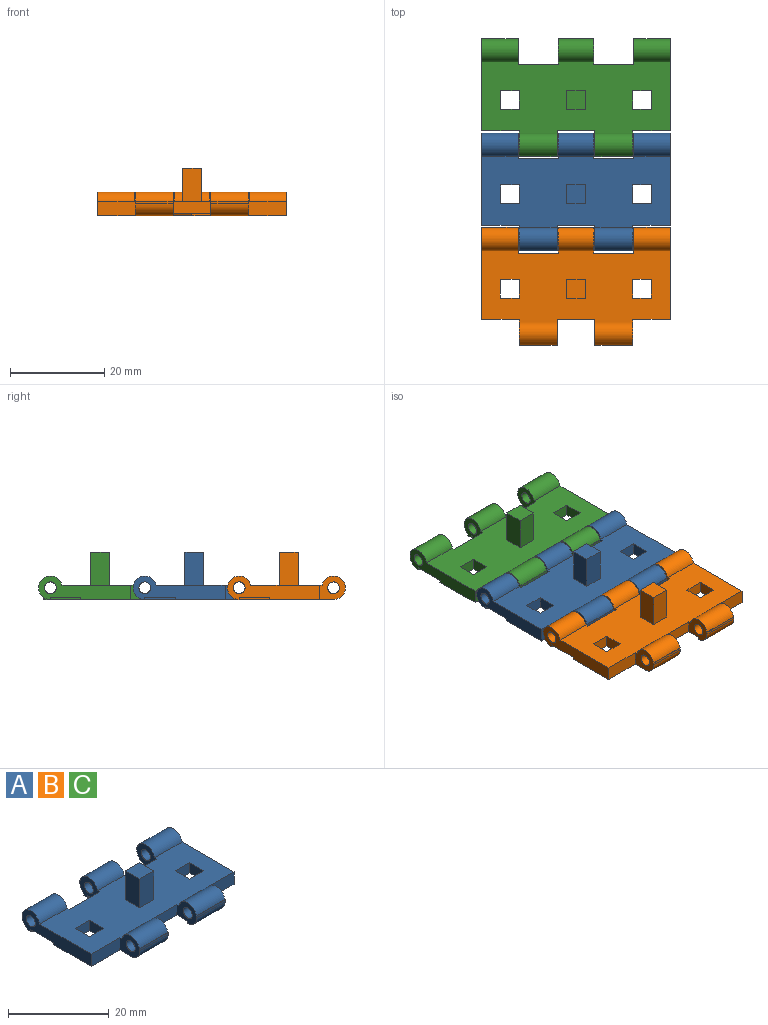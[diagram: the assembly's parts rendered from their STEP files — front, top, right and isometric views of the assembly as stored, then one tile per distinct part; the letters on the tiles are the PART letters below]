
ASSEMBLY  parts=3 mates=2
PART A: 71 faces, bbox 40x25x10 mm
  f0: plane 7.5x3.65mm, normal (0,0,-1), area 15.4mm2, adj f2,f25,f65,f66,f69
  f1: plane 40x15.1mm, normal (0,0,1), area 533.5mm2, adj f2,f6,f7,f9,f10,f11,f12,f13
  f2: plane 5.5x5mm, normal (-1,0,0), area 17.6mm2, adj f0,f1,f3,f5,f12,f21,f29,f34
  f3: cylinder r=2.5mm len=7.5mm, axis (1,0,0), area 17.7mm2, adj f2,f25,f34,f68
  f4: plane 16x13.6mm, normal (0,0,-1), area 80.5mm2, adj f6,f7,f14,f40,f52,f55,f61,f62
  f5: plane 40x17mm, normal (0,0,-1), area 277mm2, adj f2,f24,f25,f26,f49,f50,f53,f58
  f6: plane 19.5x5mm, normal (-1,0,0), area 56.4mm2, adj f1,f4,f28,f35,f47,f48,f49,f55
  f7: plane 4x3mm, normal (0,1,0), area 11.6mm2, adj f1,f4,f40,f41,f61,f64
  f8: plane 16x13.6mm, normal (0,0,-1), area 80.5mm2, adj f10,f15,f27,f38,f51,f56,f57,f59
  f9: plane 5.5x5mm, normal (-1,0,0), area 16.1mm2, adj f1,f11,f16,f31,f33,f51,f54,f57
  f10: plane 4x3mm, normal (-1,0,0), area 11.3mm2, adj f1,f8,f36,f38,f59,f60
  f11: cylinder r=2.5mm len=8mm, axis (1,0,0), area 54.8mm2, adj f1,f9,f15,f31
  f12: cylinder r=2.5mm len=7.5mm, axis (1,0,0), area 51.4mm2, adj f1,f2,f25,f29
  f13: plane 5.5x5mm, normal (1,0,0), area 16.1mm2, adj f1,f17,f18,f19,f32,f52,f54,f61
  f14: plane 5.5x5mm, normal (-1,0,0), area 17.6mm2, adj f1,f4,f17,f18,f19,f32,f52,f55
  f15: plane 5.5x5mm, normal (1,0,0), area 17.6mm2, adj f1,f8,f11,f16,f31,f33,f51,f56
  f16: cylinder r=1.25mm len=8mm, axis (1,0,0), area 62.8mm2, adj f9,f15
  f17: cylinder r=1.25mm len=8mm, axis (1,0,0), area 62.8mm2, adj f13,f14
  f18: cylinder r=2.5mm len=8mm, axis (1,0,0), area 54.8mm2, adj f1,f13,f14,f19
  f19: plane 8x0.05mm, normal (0,0,1), area 0.4mm2, adj f13,f14,f18,f32
  f20: cylinder r=1.25mm len=7.75mm, axis (1,0,0), area 60.9mm2, adj f24,f27
  f21: cylinder r=1.25mm len=7.5mm, axis (1,0,0), area 58.9mm2, adj f2,f25
  f22: cylinder r=2.5mm len=7.75mm, axis (1,0,0), area 53.1mm2, adj f1,f24,f27,f30
  f23: plane 7.75x0.5mm, normal (0,1,0), area 3.9mm2, adj f24,f27,f30,f50
  f24: plane 5.5x5mm, normal (-1,0,0), area 17.6mm2, adj f1,f5,f20,f22,f23,f30,f50,f53
  f25: plane 5.5x5mm, normal (1,0,0), area 17.6mm2, adj f0,f1,f3,f5,f12,f21,f29,f34
  f26: plane 5.5x5mm, normal (1,0,0), area 17.6mm2, adj f1,f5,f28,f35,f47,f48,f49,f67
  f27: plane 19.5x5mm, normal (1,0,0), area 56.4mm2, adj f1,f8,f20,f22,f23,f30,f50,f56
  f28: plane 7.75x0.05mm, normal (0,0,1), area 0.4mm2, adj f6,f26,f35,f48
  f29: plane 7.5x0.05mm, normal (0,0,1), area 0.4mm2, adj f2,f12,f25,f34
  f30: plane 7.75x0.05mm, normal (0,0,1), area 0.4mm2, adj f22,f23,f24,f27
  f31: plane 8x0.05mm, normal (0,0,1), area 0.4mm2, adj f9,f11,f15,f33
  f32: plane 8x0.5mm, normal (0,-1,0), area 4mm2, adj f13,f14,f19,f52
  f33: plane 8x0.5mm, normal (0,-1,0), area 4mm2, adj f9,f15,f31,f51
  f34: plane 7.5x0.5mm, normal (0,1,0), area 3.8mm2, adj f2,f3,f25,f29
  f35: plane 7.75x0.5mm, normal (0,1,0), area 3.9mm2, adj f6,f26,f28,f49
  f36: plane 4x2.5mm, normal (0,-1,0), area 10mm2, adj f1,f10,f37,f60
  f37: plane 4x2.5mm, normal (1,0,0), area 10mm2, adj f1,f36,f38,f60
  f38: plane 4x3mm, normal (0,1,0), area 11.6mm2, adj f1,f8,f10,f37,f57,f60
  f39: plane 4x2.5mm, normal (0,-1,0), area 10mm2, adj f1,f40,f41,f64
  f40: plane 4x3mm, normal (1,0,0), area 11.3mm2, adj f1,f4,f7,f39,f62,f64
  f41: plane 4x2.5mm, normal (-1,0,0), area 10mm2, adj f1,f7,f39,f64
  f42: plane 7x4mm, normal (0,-1,0), area 28mm2, adj f1,f43,f45,f46
  f43: plane 7x4mm, normal (1,0,0), area 28mm2, adj f1,f42,f44,f46
  f44: plane 7x4mm, normal (0,1,0), area 28mm2, adj f1,f43,f45,f46
  f45: plane 7x4mm, normal (-1,0,0), area 28mm2, adj f1,f42,f44,f46
  f46: plane 4x4mm, normal (0,0,1), area 16mm2, adj f42,f43,f44,f45
  f47: cylinder r=1.25mm len=7.75mm, axis (1,0,0), area 60.9mm2, adj f6,f26
  f48: cylinder r=2.5mm len=7.75mm, axis (1,0,0), area 53.1mm2, adj f1,f6,f26,f28
  f49: cylinder r=2.5mm len=7.75mm, axis (1,0,0), area 30.4mm2, adj f5,f6,f26,f35
  f50: cylinder r=2.5mm len=7.75mm, axis (1,0,0), area 30.4mm2, adj f5,f23,f24,f27
  f51: cylinder r=2.5mm len=8mm, axis (1,0,0), area 31.4mm2, adj f8,f9,f15,f33
  f52: cylinder r=2.5mm len=8mm, axis (1,0,0), area 31.4mm2, adj f4,f13,f14,f32
  f53: plane 8.5x3mm, normal (0,1,0), area 25.5mm2, adj f1,f5,f24,f25
  f54: plane 8x2.5mm, normal (0,-1,0), area 20mm2, adj f1,f9,f13,f60,f64
  f55: plane 8x3mm, normal (0,-1,0), area 24mm2, adj f1,f4,f6,f14
  f56: plane 8x3mm, normal (0,-1,0), area 24mm2, adj f1,f8,f15,f27
  f57: plane 8.82x7.5mm, normal (-0.65,0.76,0), area 5.8mm2, adj f8,f9,f38,f60
  f58: plane 20x17mm, normal (0.65,-0.76,0), area 13.1mm2, adj f5,f27,f60,f63
  f59: plane 4x3.4mm, normal (-0.65,0.76,0), area 2.6mm2, adj f8,f10,f27,f60
  f60: plane 20x20mm, normal (0,0,-1), area 97.5mm2, adj f9,f10,f27,f36,f37,f38,f54,f57
  f61: plane 8.82x7.5mm, normal (0.65,0.76,0), area 5.8mm2, adj f4,f7,f13,f64
  f62: plane 4x3.4mm, normal (0.65,0.76,0), area 2.6mm2, adj f4,f6,f40,f64
  f63: plane 20x17mm, normal (-0.65,-0.76,0), area 13.1mm2, adj f5,f6,f58,f64
  f64: plane 20x20mm, normal (0,0,-1), area 97.5mm2, adj f6,f7,f13,f39,f40,f41,f54,f61
  f65: plane 3.75x3.19mm, normal (-0.65,0.76,0), area 2.5mm2, adj f0,f5,f25,f66
  f66: plane 3.75x3.19mm, normal (0.65,0.76,0), area 2.5mm2, adj f0,f2,f5,f65
  f67: plane 8.5x3mm, normal (0,1,0), area 25.5mm2, adj f1,f2,f5,f26
  f68: plane 7.5x0.47mm, normal (0,1,0), area 3.6mm2, adj f2,f3,f25,f70
  f69: plane 7.5x0.5mm, normal (0,-1,0), area 3.8mm2, adj f0,f2,f25,f70
  f70: plane 7.5x1mm, normal (0,0,-1), area 7.5mm2, adj f2,f25,f68,f69
PART B: same geometry as A
PART C: same geometry as A
PLACE A t=(4.05,-13.47,1.68)mm
PLACE B t=(4.05,-33.47,1.68)mm
PLACE C t=(4.05,6.53,1.68)mm
MATE cylindrical A.f3 <-> C.f11  axis (1,0,0) through (-8.2,-0.97,4.18)mm
MATE cylindrical A.f11 <-> B.f3  axis (1,0,0) through (16.05,-20.97,4.18)mm
